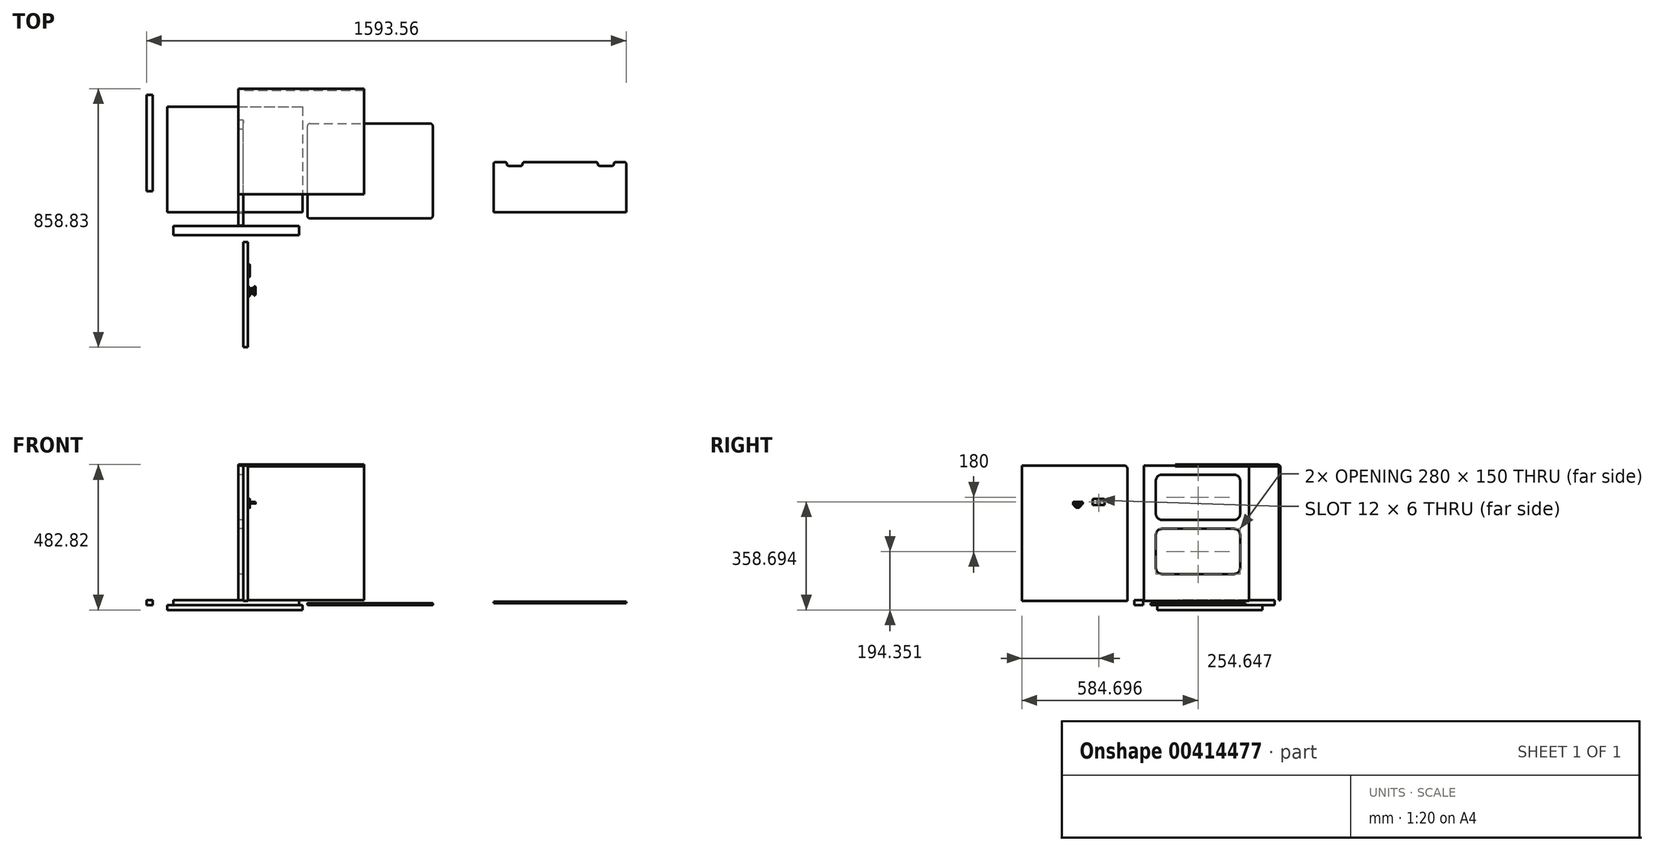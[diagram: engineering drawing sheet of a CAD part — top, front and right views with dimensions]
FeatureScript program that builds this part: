
annotation { "Feature Type Name" : "Feature", "Feature Type Description" : "" }
export const myFeature = defineFeature(function(context is Context, id is Id, definition is map)
    precondition{}
    {
        {
            var Q0;
            Q0=qCreatedBy(makeId("Top.planeOp"),FACE);
            var sketch = newSketch(context, id + "F0", { "sketchPlane" : qUnion([Q0])});
            skLineSegment(sketch, "E0.bottom", {"start": v(-256.52, 168.9) * mm, "end": v(193.48, 168.9) * mm, "construction": true});
            skLineSegment(sketch, "E0.top", {"start": v(-236.52, -151.1) * mm, "end": v(213.48, -151.1) * mm, "construction": true});
            skLineSegment(sketch, "E1.bottom", {"start": v(-236.52, 183.9) * mm, "end": v(213.48, 183.9) * mm});
            skLineSegment(sketch, "E1.top", {"start": v(-221.52, -166.1) * mm, "end": v(198.48, -166.1) * mm});
            skLineSegment(sketch, "E1.left", {"start": v(-236.52, 183.9) * mm, "end": v(-236.52, -206.1) * mm});
            skLineSegment(sketch, "E1.right", {"start": v(213.48, 183.9) * mm, "end": v(213.48, -221.1) * mm});
            skPoint(sketch, "E2.visualSharp", {"position": v(213.48, 183.9) * mm});
            skLineSegment(sketch, "E2.filletArc", {"start": v(213.48, 183.9) * mm, "end": v(213.48, 183.9) * mm});
            skPoint(sketch, "E3.visualSharp", {"position": v(213.48, -166.1) * mm});
            skPoint(sketch, "E4.visualSharp", {"position": v(-236.52, 183.9) * mm});
            skLineSegment(sketch, "E4.filletArc", {"start": v(-236.52, 183.9) * mm, "end": v(-236.52, 183.9) * mm});
            skPoint(sketch, "E5.visualSharp", {"position": v(-236.52, -166.1) * mm});
            skLineSegment(sketch, "E6", {"start": v(-221.52, -166.1) * mm, "end": v(-236.52, -166.1) * mm});
            skLineSegment(sketch, "E7", {"start": v(-236.52, -166.1) * mm, "end": v(-236.52, -151.1) * mm});
            skLineSegment(sketch, "E8", {"start": v(213.48, -151.1) * mm, "end": v(213.48, -166.1) * mm});
            skLineSegment(sketch, "E9", {"start": v(213.48, -166.1) * mm, "end": v(198.48, -166.1) * mm});
            skSolve(sketch);
        }
        {
            var Q0;
            Q0 = qSketchRegion(id + "F0", true);
            extrude(context, id + "F1", {"entities" : qUnion([Q0]), "depth" : 16 * mm});
        }
        {
            var Q0;
            Q0=qCreatedBy(makeId("Right.planeOp"),FACE);
            var sketch = newSketch(context, id + "F2", { "sketchPlane" : qUnion([Q0])});
            skLineSegment(sketch, "E10.bottom", {"start": v(-210.27, 29.35) * mm, "end": v(139.73, 29.35) * mm});
            skLineSegment(sketch, "E10.top", {"start": v(-210.27, 479.35) * mm, "end": v(129.73, 479.35) * mm});
            skLineSegment(sketch, "E10.left", {"start": v(-210.27, 29.35) * mm, "end": v(-210.27, 479.35) * mm});
            skLineSegment(sketch, "E10.right", {"start": v(139.73, 29.35) * mm, "end": v(139.73, 469.35) * mm});
            skPoint(sketch, "E11.visualSharp", {"position": v(139.73, 479.35) * mm});
            skArc(sketch, "E11.filletArc", {"start": v(139.73, 469.35) * mm, "mid": v(136.8, 476.42) * mm, "end": v(129.73, 479.35) * mm});
            skLineSegment(sketch, "E12.bottom", {"start": v(-150.27, 269.35) * mm, "end": v(89.73, 269.35) * mm});
            skLineSegment(sketch, "E12.top", {"start": v(-150.27, 119.35) * mm, "end": v(89.73, 119.35) * mm});
            skLineSegment(sketch, "E12.left", {"start": v(-170.27, 249.35) * mm, "end": v(-170.27, 139.35) * mm});
            skLineSegment(sketch, "E12.right", {"start": v(109.73, 249.35) * mm, "end": v(109.73, 139.35) * mm});
            skLineSegment(sketch, "E13.bottom", {"start": v(-150.27, 449.35) * mm, "end": v(89.73, 449.35) * mm});
            skLineSegment(sketch, "E13.top", {"start": v(-150.27, 299.35) * mm, "end": v(89.73, 299.35) * mm});
            skLineSegment(sketch, "E13.left", {"start": v(-170.27, 429.35) * mm, "end": v(-170.27, 319.35) * mm});
            skLineSegment(sketch, "E13.right", {"start": v(109.73, 429.35) * mm, "end": v(109.73, 319.35) * mm});
            skPoint(sketch, "E14.visualSharp", {"position": v(109.73, 449.35) * mm});
            skArc(sketch, "E14.filletArc", {"start": v(109.73, 429.35) * mm, "mid": v(103.87, 443.5) * mm, "end": v(89.73, 449.35) * mm});
            skPoint(sketch, "E15.visualSharp", {"position": v(-170.27, 449.35) * mm});
            skArc(sketch, "E15.filletArc", {"start": v(-150.27, 449.35) * mm, "mid": v(-164.42, 443.5) * mm, "end": v(-170.27, 429.35) * mm});
            skPoint(sketch, "E16.visualSharp", {"position": v(-170.27, 299.35) * mm});
            skArc(sketch, "E16.filletArc", {"start": v(-170.27, 319.35) * mm, "mid": v(-164.42, 305.2) * mm, "end": v(-150.27, 299.35) * mm});
            skPoint(sketch, "E17.visualSharp", {"position": v(109.73, 299.35) * mm});
            skArc(sketch, "E17.filletArc", {"start": v(89.73, 299.35) * mm, "mid": v(103.87, 305.2) * mm, "end": v(109.73, 319.35) * mm});
            skPoint(sketch, "E18.visualSharp", {"position": v(109.73, 269.35) * mm});
            skArc(sketch, "E18.filletArc", {"start": v(109.73, 249.35) * mm, "mid": v(103.87, 263.5) * mm, "end": v(89.73, 269.35) * mm});
            skPoint(sketch, "E19.visualSharp", {"position": v(109.73, 119.35) * mm});
            skArc(sketch, "E19.filletArc", {"start": v(89.73, 119.35) * mm, "mid": v(103.87, 125.2) * mm, "end": v(109.73, 139.35) * mm});
            skPoint(sketch, "E20.visualSharp", {"position": v(-170.27, 119.35) * mm});
            skArc(sketch, "E20.filletArc", {"start": v(-170.27, 139.35) * mm, "mid": v(-164.42, 125.2) * mm, "end": v(-150.27, 119.35) * mm});
            skPoint(sketch, "E21.visualSharp", {"position": v(-170.27, 269.35) * mm});
            skArc(sketch, "E21.filletArc", {"start": v(-150.27, 269.35) * mm, "mid": v(-164.42, 263.5) * mm, "end": v(-170.27, 249.35) * mm});
            skSolve(sketch);
        }
        {
            var Q0;
            Q0 = qSketchRegion(id + "F2", true);
            extrude(context, id + "F3", {"entities" : qUnion([Q0]), "depth" : 16 * mm});
        }
        {
            var Q0;
            Q0=qCreatedBy(makeId("Right.planeOp"),FACE);
            var sketch = newSketch(context, id + "F4", { "sketchPlane" : qUnion([Q0])});
            skLineSegment(sketch, "E22", {"start": v(243.86, 32.82) * mm, "end": v(243.86, 472.82) * mm});
            skLineSegment(sketch, "E23", {"start": v(233.86, 482.82) * mm, "end": v(-106.14, 482.82) * mm});
            skPoint(sketch, "E24.visualSharp", {"position": v(243.86, 482.82) * mm});
            skArc(sketch, "E24.filletArc", {"start": v(243.86, 472.82) * mm, "mid": v(240.93, 479.9) * mm, "end": v(233.86, 482.82) * mm});
            skLineSegment(sketch, "E25", {"start": v(243.86, 32.82) * mm, "end": v(237.86, 32.82) * mm});
            skLineSegment(sketch, "E26", {"start": v(237.86, 32.82) * mm, "end": v(237.86, 472.82) * mm});
            skLineSegment(sketch, "E27", {"start": v(233.86, 476.82) * mm, "end": v(-106.14, 476.82) * mm});
            skLineSegment(sketch, "E28", {"start": v(-106.14, 476.82) * mm, "end": v(-106.14, 482.82) * mm});
            skPoint(sketch, "E29.visualSharp", {"position": v(237.86, 476.82) * mm});
            skArc(sketch, "E29.filletArc", {"start": v(237.86, 472.82) * mm, "mid": v(236.69, 475.65) * mm, "end": v(233.86, 476.82) * mm});
            skSolve(sketch);
        }
        {
            var Q0;
            Q0 = qSketchRegion(id + "F4", true);
            extrude(context, id + "F5", {"entities" : qUnion([Q0]), "depth" : 418 * mm});
        }
        {
            var Q0;
            Q0=makeQuery(id+"F3.opExtrude","CAP_FACE",FACE,{"disambiguationData":[OSD([sQuery(id+"F2.wireOp",EDGE,"E10.bottom"),sQuery(id+"F2.wireOp",EDGE,"E10.top"),sQuery(id+"F2.wireOp",EDGE,"E10.left"),sQuery(id+"F2.wireOp",EDGE,"E10.right"),sQuery(id+"F2.wireOp",EDGE,"E11.filletArc"),sQuery(id+"F2.wireOp",EDGE,"E12.bottom"),sQuery(id+"F2.wireOp",EDGE,"E12.top"),sQuery(id+"F2.wireOp",EDGE,"E12.left"),sQuery(id+"F2.wireOp",EDGE,"E12.right"),sQuery(id+"F2.wireOp",EDGE,"E13.bottom"),sQuery(id+"F2.wireOp",EDGE,"E13.top"),sQuery(id+"F2.wireOp",EDGE,"E13.left"),sQuery(id+"F2.wireOp",EDGE,"E13.right"),sQuery(id+"F2.wireOp",EDGE,"E14.filletArc"),sQuery(id+"F2.wireOp",EDGE,"E15.filletArc"),sQuery(id+"F2.wireOp",EDGE,"E16.filletArc"),sQuery(id+"F2.wireOp",EDGE,"E17.filletArc"),sQuery(id+"F2.wireOp",EDGE,"E18.filletArc"),sQuery(id+"F2.wireOp",EDGE,"E19.filletArc"),sQuery(id+"F2.wireOp",EDGE,"E20.filletArc"),sQuery(id+"F2.wireOp",EDGE,"E21.filletArc")])],"isStart":false});
            var sketch = newSketch(context, id + "F6", { "sketchPlane" : qUnion([Q0])});
            skLineSegment(sketch, "E30.bottom", {"start": v(-614.97, 29.35) * mm, "end": v(-264.97, 29.35) * mm});
            skLineSegment(sketch, "E30.top", {"start": v(-614.97, 479.35) * mm, "end": v(-274.97, 479.35) * mm});
            skLineSegment(sketch, "E30.left", {"start": v(-614.97, 29.35) * mm, "end": v(-614.97, 479.35) * mm});
            skLineSegment(sketch, "E30.right", {"start": v(-264.97, 29.35) * mm, "end": v(-264.97, 469.35) * mm});
            skArc(sketch, "E31.filletArc", {"start": v(-264.97, 469.35) * mm, "mid": v(-267.9, 476.42) * mm, "end": v(-274.97, 479.35) * mm});
            skSolve(sketch);
        }
        {
            var Q0;
            Q0 = qSketchRegion(id + "F6", true);
            extrude(context, id + "F7", {"entities" : qUnion([Q0]), "depth" : 16 * mm});
        }
        {
            var Q0;
            Q0=makeQuery(id+"F1.opExtrude","CAP_FACE",FACE,{"disambiguationData":[OSD([sQuery(id+"F0.wireOp",EDGE,"E1.bottom"),sQuery(id+"F0.wireOp",EDGE,"E1.top"),sQuery(id+"F0.wireOp",EDGE,"E1.left"),sQuery(id+"F0.wireOp",EDGE,"E1.right"),sQuery(id+"F0.wireOp",EDGE,"E6"),sQuery(id+"F0.wireOp",EDGE,"E7"),sQuery(id+"F0.wireOp",EDGE,"E8"),sQuery(id+"F0.wireOp",EDGE,"E9")])],"isStart":false});
            var sketch = newSketch(context, id + "F8", { "sketchPlane" : qUnion([Q0])});
            skLineSegment(sketch, "E32.bottom", {"start": v(-216.2, -212.1) * mm, "end": v(201.8, -212.1) * mm});
            skLineSegment(sketch, "E32.top", {"start": v(-216.2, -242.1) * mm, "end": v(201.8, -242.1) * mm});
            skLineSegment(sketch, "E32.left", {"start": v(-216.2, -212.1) * mm, "end": v(-216.2, -242.1) * mm});
            skLineSegment(sketch, "E32.right", {"start": v(201.8, -212.1) * mm, "end": v(201.8, -242.1) * mm});
            skSolve(sketch);
        }
        {
            var Q0;
            Q0 = qSketchRegion(id + "F8", true);
            extrude(context, id + "F9", {"entities" : qUnion([Q0]), "depth" : 16 * mm});
        }
        {
            var Q0;
            Q0=makeQuery(id+"F1.opExtrude","CAP_FACE",FACE,{"disambiguationData":[OSD([sQuery(id+"F0.wireOp",EDGE,"E1.bottom"),sQuery(id+"F0.wireOp",EDGE,"E1.top"),sQuery(id+"F0.wireOp",EDGE,"E1.left"),sQuery(id+"F0.wireOp",EDGE,"E1.right"),sQuery(id+"F0.wireOp",EDGE,"E6"),sQuery(id+"F0.wireOp",EDGE,"E7"),sQuery(id+"F0.wireOp",EDGE,"E8"),sQuery(id+"F0.wireOp",EDGE,"E9")])],"isStart":false});
            var sketch = newSketch(context, id + "F10", { "sketchPlane" : qUnion([Q0])});
            skLineSegment(sketch, "E33.bottom", {"start": v(-285.24, 223.93) * mm, "end": v(-305.24, 223.93) * mm});
            skLineSegment(sketch, "E33.top", {"start": v(-285.24, -96.07) * mm, "end": v(-305.24, -96.07) * mm});
            skLineSegment(sketch, "E33.left", {"start": v(-285.24, 223.93) * mm, "end": v(-285.24, -96.07) * mm});
            skLineSegment(sketch, "E33.right", {"start": v(-305.24, 223.93) * mm, "end": v(-305.24, -96.07) * mm});
            skSolve(sketch);
        }
        {
            var Q0;
            Q0 = qSketchRegion(id + "F10", true);
            extrude(context, id + "F11", {"entities" : qUnion([Q0]), "depth" : 16 * mm});
        }
        {
            var Q0;
            Q0=makeQuery(id+"F1.opExtrude","CAP_FACE",FACE,{"disambiguationData":[OSD([sQuery(id+"F0.wireOp",EDGE,"E1.bottom"),sQuery(id+"F0.wireOp",EDGE,"E1.top"),sQuery(id+"F0.wireOp",EDGE,"E1.left"),sQuery(id+"F0.wireOp",EDGE,"E1.right"),sQuery(id+"F0.wireOp",EDGE,"E6"),sQuery(id+"F0.wireOp",EDGE,"E7"),sQuery(id+"F0.wireOp",EDGE,"E8"),sQuery(id+"F0.wireOp",EDGE,"E9")])],"isStart":false});
            var sketch = newSketch(context, id + "F12", { "sketchPlane" : qUnion([Q0])});
            skLineSegment(sketch, "E34.bottom", {"start": v(237.71, -186.82) * mm, "end": v(637.71, -186.82) * mm});
            skLineSegment(sketch, "E34.top", {"start": v(237.71, 128.18) * mm, "end": v(637.71, 128.18) * mm});
            skLineSegment(sketch, "E34.left", {"start": v(229.71, -178.82) * mm, "end": v(229.71, 120.18) * mm});
            skLineSegment(sketch, "E34.right", {"start": v(645.71, -178.82) * mm, "end": v(645.71, 120.18) * mm});
            skPoint(sketch, "E35.visualSharp", {"position": v(229.71, 128.18) * mm});
            skArc(sketch, "E35.filletArc", {"start": v(237.71, 128.18) * mm, "mid": v(232.06, 125.84) * mm, "end": v(229.71, 120.18) * mm});
            skPoint(sketch, "E36.visualSharp", {"position": v(645.71, 128.18) * mm});
            skArc(sketch, "E36.filletArc", {"start": v(645.71, 120.18) * mm, "mid": v(643.37, 125.84) * mm, "end": v(637.71, 128.18) * mm});
            skPoint(sketch, "E37.visualSharp", {"position": v(645.71, -186.82) * mm});
            skArc(sketch, "E37.filletArc", {"start": v(637.71, -186.82) * mm, "mid": v(643.37, -184.48) * mm, "end": v(645.71, -178.82) * mm});
            skPoint(sketch, "E38.visualSharp", {"position": v(229.71, -186.82) * mm});
            skArc(sketch, "E38.filletArc", {"start": v(229.71, -178.82) * mm, "mid": v(232.06, -184.48) * mm, "end": v(237.71, -186.82) * mm});
            skSolve(sketch);
        }
        {
            var Q0;
            Q0 = qSketchRegion(id + "F12", true);
            extrude(context, id + "F13", {"entities" : qUnion([Q0]), "depth" : 6 * mm});
        }
        {
            var Q0;
            Q0=makeQuery(id+"F13.opExtrude","CAP_FACE",FACE,{"disambiguationData":[OSD([sQuery(id+"F12.wireOp",EDGE,"E34.bottom"),sQuery(id+"F12.wireOp",EDGE,"E34.top"),sQuery(id+"F12.wireOp",EDGE,"E34.left"),sQuery(id+"F12.wireOp",EDGE,"E34.right"),sQuery(id+"F12.wireOp",EDGE,"E35.filletArc"),sQuery(id+"F12.wireOp",EDGE,"E36.filletArc"),sQuery(id+"F12.wireOp",EDGE,"E37.filletArc"),sQuery(id+"F12.wireOp",EDGE,"E38.filletArc")])],"isStart":false});
            var sketch = newSketch(context, id + "F14", { "sketchPlane" : qUnion([Q0])});
            skLineSegment(sketch, "E39.bottom", {"start": v(848.32, -166) * mm, "end": v(1288.32, -166) * mm});
            skLineSegment(sketch, "E39.top", {"start": v(853.32, 0) * mm, "end": v(887.01, 0) * mm});
            skLineSegment(sketch, "E39.left", {"start": v(848.32, -166) * mm, "end": v(848.32, -5) * mm});
            skLineSegment(sketch, "E39.right", {"start": v(1288.32, -166) * mm, "end": v(1288.32, -5) * mm});
            skPoint(sketch, "E40.visualSharp", {"position": v(848.32, 0) * mm});
            skArc(sketch, "E40.filletArc", {"start": v(853.32, 0) * mm, "mid": v(849.79, -1.46) * mm, "end": v(848.32, -5) * mm});
            skPoint(sketch, "E41.visualSharp", {"position": v(1288.32, 0) * mm});
            skArc(sketch, "E41.filletArc", {"start": v(1288.32, -5) * mm, "mid": v(1286.86, -1.46) * mm, "end": v(1283.32, 0) * mm});
            skLineSegment(sketch, "E42", {"start": v(897.52, -12) * mm, "end": v(939.13, -12) * mm});
            skLineSegment(sketch, "E43", {"start": v(1199.52, -12) * mm, "end": v(1242.13, -12) * mm});
            skLineSegment(sketch, "E44.trimOffspring", {"start": v(949.63, 0) * mm, "end": v(1189.01, 0) * mm});
            skLineSegment(sketch, "E45.trimOffspring", {"start": v(1252.63, 0) * mm, "end": v(1283.32, 0) * mm});
            skLineSegment(sketch, "E46", {"start": v(892.6, -7.87) * mm, "end": v(891.94, -4.13) * mm});
            skLineSegment(sketch, "E47", {"start": v(944.05, -7.87) * mm, "end": v(944.71, -4.13) * mm});
            skLineSegment(sketch, "E48", {"start": v(1193.94, -4.13) * mm, "end": v(1194.6, -7.87) * mm});
            skLineSegment(sketch, "E49", {"start": v(1247.71, -4.13) * mm, "end": v(1247.05, -7.87) * mm});
            skPoint(sketch, "E50.visualSharp", {"position": v(891.2, 0) * mm});
            skArc(sketch, "E50.filletArc", {"start": v(891.94, -4.13) * mm, "mid": v(890.23, -1.17) * mm, "end": v(887.01, 0) * mm});
            skPoint(sketch, "E51.visualSharp", {"position": v(893.32, -12) * mm});
            skArc(sketch, "E51.filletArc", {"start": v(892.6, -7.87) * mm, "mid": v(894.3, -10.83) * mm, "end": v(897.52, -12) * mm});
            skPoint(sketch, "E52.visualSharp", {"position": v(943.32, -12) * mm});
            skArc(sketch, "E52.filletArc", {"start": v(939.13, -12) * mm, "mid": v(942.34, -10.83) * mm, "end": v(944.05, -7.87) * mm});
            skPoint(sketch, "E53.visualSharp", {"position": v(945.44, 0) * mm});
            skArc(sketch, "E53.filletArc", {"start": v(949.63, 0) * mm, "mid": v(946.42, -1.17) * mm, "end": v(944.71, -4.13) * mm});
            skPoint(sketch, "E54.visualSharp", {"position": v(1193.2, 0) * mm});
            skArc(sketch, "E54.filletArc", {"start": v(1193.94, -4.13) * mm, "mid": v(1192.23, -1.17) * mm, "end": v(1189.01, 0) * mm});
            skPoint(sketch, "E55.visualSharp", {"position": v(1195.32, -12) * mm});
            skArc(sketch, "E55.filletArc", {"start": v(1194.6, -7.87) * mm, "mid": v(1196.3, -10.83) * mm, "end": v(1199.52, -12) * mm});
            skPoint(sketch, "E56.visualSharp", {"position": v(1246.32, -12) * mm});
            skArc(sketch, "E56.filletArc", {"start": v(1242.13, -12) * mm, "mid": v(1245.34, -10.83) * mm, "end": v(1247.05, -7.87) * mm});
            skPoint(sketch, "E57.visualSharp", {"position": v(1248.44, 0) * mm});
            skArc(sketch, "E57.filletArc", {"start": v(1252.63, 0) * mm, "mid": v(1249.42, -1.17) * mm, "end": v(1247.71, -4.13) * mm});
            skSolve(sketch);
        }
        {
            var Q0;
            Q0 = qSketchRegion(id + "F14", true);
            extrude(context, id + "F15", {"entities" : qUnion([Q0]), "depth" : 6 * mm});
        }
        {
            var Q0;
            Q0=makeQuery(id+"F7.opExtrude","CAP_FACE",FACE,{"disambiguationData":[OSD([sQuery(id+"F6.wireOp",EDGE,"E30.bottom"),sQuery(id+"F6.wireOp",EDGE,"E30.top"),sQuery(id+"F6.wireOp",EDGE,"E30.left"),sQuery(id+"F6.wireOp",EDGE,"E30.right"),sQuery(id+"F6.wireOp",EDGE,"E31.filletArc")])],"isStart":false});
            var sketch = newSketch(context, id + "F16", { "sketchPlane" : qUnion([Q0])});
            skLineSegment(sketch, "E58", {"start": v(-445.4, 359.4) * mm, "end": v(-439.4, 359.4) * mm});
            skLineSegment(sketch, "E59", {"start": v(-415.4, 359.4) * mm, "end": v(-415.4, 351.05) * mm});
            skLineSegment(sketch, "E60", {"start": v(-416.57, 348.22) * mm, "end": v(-424.23, 340.57) * mm});
            skLineSegment(sketch, "E61", {"start": v(-427.06, 339.4) * mm, "end": v(-433.74, 339.4) * mm});
            skLineSegment(sketch, "E62", {"start": v(-436.57, 340.57) * mm, "end": v(-444.23, 348.22) * mm});
            skLineSegment(sketch, "E63", {"start": v(-445.4, 351.05) * mm, "end": v(-445.4, 359.4) * mm});
            skCircle(sketch, "E64", {"center": v(-430.4, 347.4) * mm, "radius": 3 * mm});
            skPoint(sketch, "E64.centerSnap0", {"position": v(-430.4, 339.4) * mm});
            skLineSegment(sketch, "E65", {"start": v(-439.4, 359.4) * mm, "end": v(-439.4, 353.4) * mm});
            skLineSegment(sketch, "E66", {"start": v(-439.4, 353.4) * mm, "end": v(-433.4, 353.4) * mm});
            skLineSegment(sketch, "E67", {"start": v(-433.4, 353.4) * mm, "end": v(-433.4, 359.4) * mm});
            skLineSegment(sketch, "E68", {"start": v(-427.4, 359.4) * mm, "end": v(-427.4, 353.4) * mm});
            skLineSegment(sketch, "E69", {"start": v(-427.4, 353.4) * mm, "end": v(-421.4, 353.4) * mm});
            skLineSegment(sketch, "E70", {"start": v(-421.4, 353.4) * mm, "end": v(-421.4, 359.4) * mm});
            skLineSegment(sketch, "E71.trimOffspring", {"start": v(-433.4, 359.4) * mm, "end": v(-427.4, 359.4) * mm});
            skLineSegment(sketch, "E72.trimOffspring", {"start": v(-421.4, 359.4) * mm, "end": v(-415.4, 359.4) * mm});
            skPoint(sketch, "E73.visualSharp", {"position": v(-435.4, 339.4) * mm});
            skArc(sketch, "E73.filletArc", {"start": v(-436.57, 340.57) * mm, "mid": v(-435.27, 339.7) * mm, "end": v(-433.74, 339.4) * mm});
            skPoint(sketch, "E74.visualSharp", {"position": v(-425.4, 339.4) * mm});
            skArc(sketch, "E74.filletArc", {"start": v(-427.06, 339.4) * mm, "mid": v(-425.53, 339.7) * mm, "end": v(-424.23, 340.57) * mm});
            skPoint(sketch, "E75.visualSharp", {"position": v(-415.4, 349.4) * mm});
            skArc(sketch, "E75.filletArc", {"start": v(-416.57, 348.22) * mm, "mid": v(-415.7, 349.52) * mm, "end": v(-415.4, 351.05) * mm});
            skPoint(sketch, "E76.visualSharp", {"position": v(-445.4, 349.4) * mm});
            skArc(sketch, "E76.filletArc", {"start": v(-445.4, 351.05) * mm, "mid": v(-445.1, 349.52) * mm, "end": v(-444.23, 348.22) * mm});
            skSolve(sketch);
        }
        {
            var Q0;
            Q0 = qSketchRegion(id + "F16", true);
            extrude(context, id + "F17", {"entities" : qUnion([Q0]), "depth" : 6 * mm});
        }
        {
            var Q0;
            Q0=makeQuery(id+"F17.opExtrude","SWEPT_FACE",FACE,{"disambiguationData":[OSD([sQuery(id+"F16.wireOp",EDGE,"E69")])]});
            var sketch = newSketch(context, id + "F18", { "sketchPlane" : qUnion([Q0])});
            skLineSegment(sketch, "E77.bottom", {"start": v(51.37, -412.67) * mm, "end": v(53.37, -412.67) * mm});
            skLineSegment(sketch, "E77.top", {"start": v(51.37, -442.67) * mm, "end": v(53.37, -442.67) * mm});
            skLineSegment(sketch, "E77.left", {"start": v(51.37, -412.67) * mm, "end": v(51.37, -418.67) * mm});
            skLineSegment(sketch, "E77.right", {"start": v(57.37, -416.67) * mm, "end": v(57.37, -438.67) * mm});
            skLineSegment(sketch, "E78", {"start": v(51.37, -418.67) * mm, "end": v(42.37, -418.67) * mm});
            skLineSegment(sketch, "E79", {"start": v(42.37, -418.67) * mm, "end": v(42.37, -424.67) * mm});
            skLineSegment(sketch, "E80", {"start": v(42.37, -424.67) * mm, "end": v(51.37, -424.67) * mm});
            skLineSegment(sketch, "E81", {"start": v(51.37, -430.67) * mm, "end": v(42.37, -430.67) * mm});
            skLineSegment(sketch, "E82", {"start": v(42.37, -430.67) * mm, "end": v(42.37, -436.67) * mm});
            skLineSegment(sketch, "E83", {"start": v(42.37, -436.67) * mm, "end": v(51.37, -436.67) * mm});
            skLineSegment(sketch, "E84.trimOffspring", {"start": v(51.37, -436.67) * mm, "end": v(51.37, -442.67) * mm});
            skLineSegment(sketch, "E85.trimOffspring", {"start": v(51.37, -424.67) * mm, "end": v(51.37, -430.67) * mm});
            skPoint(sketch, "E86.visualSharp", {"position": v(57.37, -412.67) * mm});
            skArc(sketch, "E86.filletArc", {"start": v(57.37, -416.67) * mm, "mid": v(56.2, -413.85) * mm, "end": v(53.37, -412.67) * mm});
            skPoint(sketch, "E87.visualSharp", {"position": v(57.37, -442.67) * mm});
            skArc(sketch, "E87.filletArc", {"start": v(53.37, -442.67) * mm, "mid": v(56.2, -441.5) * mm, "end": v(57.37, -438.67) * mm});
            skSolve(sketch);
        }
        {
            var Q0;
            Q0 = qSketchRegion(id + "F18", true);
            extrude(context, id + "F19", {"entities" : qUnion([Q0]), "depth" : 6 * mm});
        }
        {
            var Q0;
            Q0=makeQuery(id+"F7.opExtrude","CAP_FACE",FACE,{"disambiguationData":[OSD([sQuery(id+"F6.wireOp",EDGE,"E30.bottom"),sQuery(id+"F6.wireOp",EDGE,"E30.top"),sQuery(id+"F6.wireOp",EDGE,"E30.left"),sQuery(id+"F6.wireOp",EDGE,"E30.right"),sQuery(id+"F6.wireOp",EDGE,"E31.filletArc")])],"isStart":false});
            var sketch = newSketch(context, id + "F20", { "sketchPlane" : qUnion([Q0])});
            skLineSegment(sketch, "E88.bottom", {"start": v(-377.32, 368.44) * mm, "end": v(-343.32, 368.44) * mm});
            skLineSegment(sketch, "E88.top", {"start": v(-380.32, 348.44) * mm, "end": v(-340.32, 348.44) * mm});
            skLineSegment(sketch, "E88.left", {"start": v(-380.32, 365.44) * mm, "end": v(-380.32, 348.44) * mm});
            skLineSegment(sketch, "E88.right", {"start": v(-340.32, 365.44) * mm, "end": v(-340.32, 348.44) * mm});
            skLineSegment(sketch, "E89.bottom", {"start": v(-360.32, 364.7) * mm, "end": v(-360.32, 364.7) * mm});
            skLineSegment(sketch, "E89.top", {"start": v(-360.32, 352.7) * mm, "end": v(-360.32, 352.7) * mm});
            skLineSegment(sketch, "E89.left", {"start": v(-357.32, 361.7) * mm, "end": v(-357.32, 355.7) * mm});
            skLineSegment(sketch, "E89.right", {"start": v(-363.32, 361.7) * mm, "end": v(-363.32, 355.7) * mm});
            skPoint(sketch, "E89.middle", {"position": v(-360.32, 358.7) * mm});
            skPoint(sketch, "E89.middle.positionSnap0", {"position": v(-360.32, 368.44) * mm});
            skPoint(sketch, "E89.centerSnap0", {"position": v(-360.32, 368.44) * mm});
            skPoint(sketch, "E90.visualSharp", {"position": v(-340.32, 368.44) * mm});
            skArc(sketch, "E90.filletArc", {"start": v(-340.32, 365.44) * mm, "mid": v(-341.2, 367.56) * mm, "end": v(-343.32, 368.44) * mm});
            skPoint(sketch, "E91.visualSharp", {"position": v(-380.32, 368.44) * mm});
            skArc(sketch, "E91.filletArc", {"start": v(-377.32, 368.44) * mm, "mid": v(-379.44, 367.56) * mm, "end": v(-380.32, 365.44) * mm});
            skPoint(sketch, "E92.visualSharp", {"position": v(-363.32, 364.7) * mm});
            skArc(sketch, "E92.filletArc", {"start": v(-360.32, 364.7) * mm, "mid": v(-362.44, 363.82) * mm, "end": v(-363.32, 361.7) * mm});
            skPoint(sketch, "E93.visualSharp", {"position": v(-357.32, 364.7) * mm});
            skArc(sketch, "E93.filletArc", {"start": v(-357.32, 361.7) * mm, "mid": v(-358.2, 363.82) * mm, "end": v(-360.32, 364.7) * mm});
            skPoint(sketch, "E94.visualSharp", {"position": v(-363.32, 352.7) * mm});
            skArc(sketch, "E94.filletArc", {"start": v(-363.32, 355.7) * mm, "mid": v(-362.44, 353.57) * mm, "end": v(-360.32, 352.7) * mm});
            skPoint(sketch, "E95.visualSharp", {"position": v(-357.32, 352.7) * mm});
            skArc(sketch, "E95.filletArc", {"start": v(-360.32, 352.7) * mm, "mid": v(-358.2, 353.57) * mm, "end": v(-357.32, 355.7) * mm});
            skSolve(sketch);
        }
        {
            var Q0;
            Q0 = qSketchRegion(id + "F20", true);
            extrude(context, id + "F21", {"entities" : qUnion([Q0]), "depth" : 6 * mm, "offsetDistance" : 25 * mm});
        }
    });
